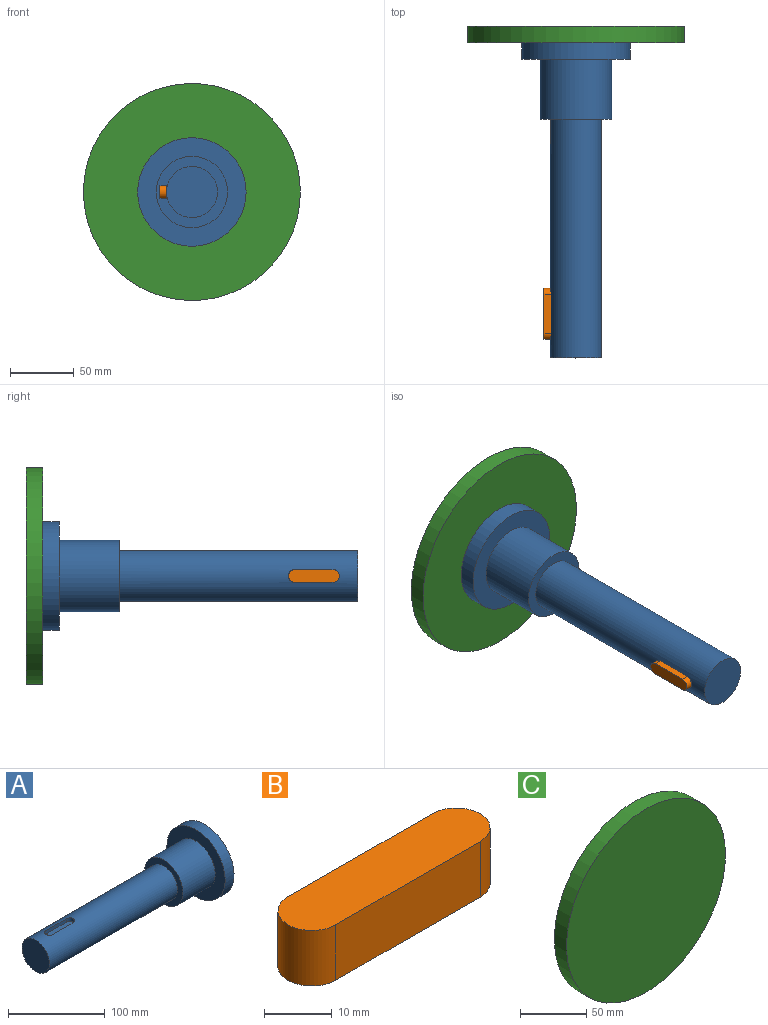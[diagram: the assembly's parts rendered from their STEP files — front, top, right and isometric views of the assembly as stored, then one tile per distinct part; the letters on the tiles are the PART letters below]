
ASSEMBLY  parts=3 mates=2
PART A: 12 faces, bbox 247x85x85 mm
  f0: cylinder r=20mm len=187mm, axis (1,0,0), area 23116.7mm2, adj f3,f4,f7,f8,f9,f10
  f1: plane 85x85mm, normal (-1,0,0), area 3211.5mm2, adj f2,f6
  f2: cylinder r=28mm len=56mm, axis (1,0,0), area 8268.7mm2, adj f1,f3
  f3: plane 56x56mm, normal (-1,0,0), area 1206.4mm2, adj f0,f2
  f4: plane 40x40mm, normal (-1,0,0), area 1256.6mm2, adj f0
  f5: plane 85x85mm, normal (1,0,0), area 5674.5mm2, adj f6
  f6: cylinder r=42.5mm len=85mm, axis (1,0,0), area 3471.5mm2, adj f1,f5
  f7: plane 30x4.37mm, normal (0,-1,0), area 130.9mm2, adj f0,f8,f10,f11
  f8: cylinder r=5mm len=10mm, axis (0,0,1), area 73.6mm2, adj f0,f7,f9,f11
  f9: plane 30x4.37mm, normal (0,1,0), area 130.9mm2, adj f0,f8,f10,f11
  f10: cylinder r=5mm len=10mm, axis (0,0,1), area 73.6mm2, adj f0,f7,f9,f11
  f11: plane 40x10mm, normal (0,0,1), area 378.5mm2, adj f7,f8,f9,f10
PART B: 6 faces, bbox 40x10x10 mm
  f0: plane 30x10mm, normal (0,1,0), area 300mm2, adj f1,f3,f4,f5
  f1: cylinder r=5mm len=10mm, axis (0,0,-1), area 157.1mm2, adj f0,f2,f4,f5
  f2: plane 30x10mm, normal (0,-1,0), area 300mm2, adj f1,f3,f4,f5
  f3: cylinder r=5mm len=10mm, axis (0,0,-1), area 157.1mm2, adj f0,f2,f4,f5
  f4: plane 40x10mm, normal (0,0,1), area 378.5mm2, adj f0,f1,f2,f3
  f5: plane 40x10mm, normal (0,0,-1), area 378.5mm2, adj f0,f1,f2,f3
PART C: 3 faces, bbox 170x13x170 mm
  f0: cylinder r=85mm len=170mm, axis (0,1,0), area 6942.9mm2, adj f1,f2
  f1: plane 170x170mm, normal (0,-1,0), area 22698mm2, adj f0
  f2: plane 170x170mm, normal (0,1,0), area 22698mm2, adj f0
PLACE A rot(axis=(-0.58,-0.58,0.58),120deg) t=(11.02,-6.38,80.65)mm
PLACE B rot(axis=(-0.58,-0.58,0.58),120deg) t=(-3.98,-6.38,80.65)mm
PLACE C t=(11.02,66.62,80.65)mm
MATE fastened A.f0 <-> C.f0  axis (0,1,0) through (11.02,53.62,80.65)mm
MATE planar B.f1 <-> A.f8  axis (1,0,0) through (-3.98,-173.88,80.65)mm
